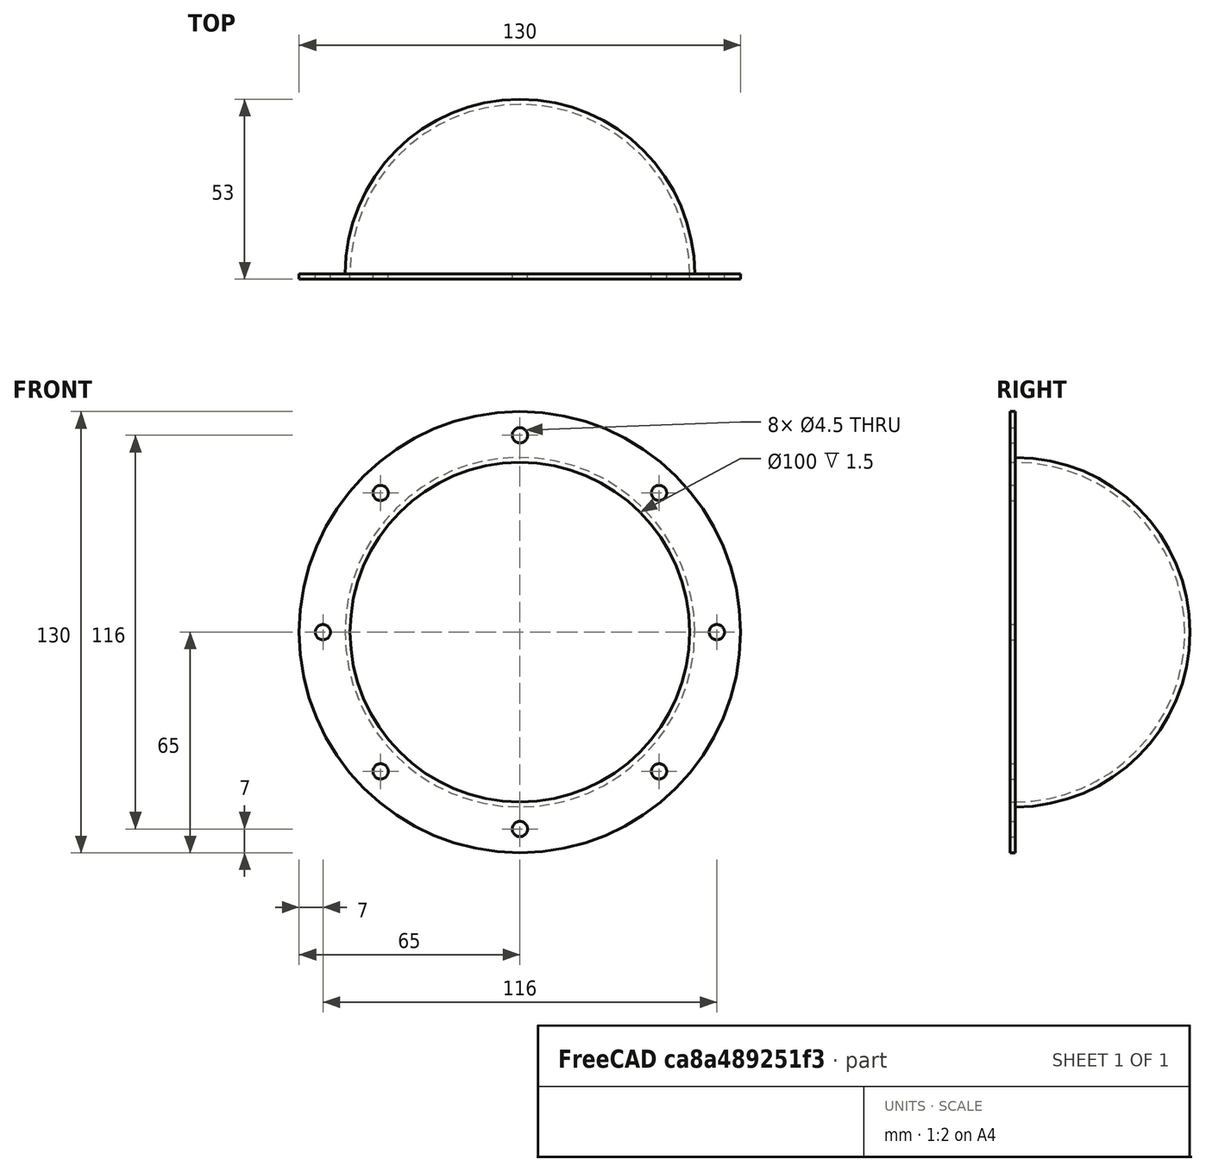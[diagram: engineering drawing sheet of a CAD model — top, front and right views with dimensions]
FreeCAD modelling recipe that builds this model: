
FCSTD DOCUMENT  (FreeCAD 0.18.4R)
Label: kuppel_LightDome
License: All rights reserved
LicenseURL: http://en.wikipedia.org/wiki/All_rights_reserved
objects: TechDraw::DrawViewDimension×4, TechDraw::DrawProjGroupItem×3, Sketcher::SketchObject×2, TechDraw::DrawSVGTemplate×2, TechDraw::DrawPage×2, Spreadsheet::Sheet×1, PartDesign::Revolution×1, TechDraw::DrawViewAnnotation×1, PartDesign::Hole×1, PartDesign::Body×1, TechDraw::DrawProjGroup×1, TechDraw::DrawViewPart×1, TechDraw::DrawGeomHatch×1
note: 7 computed .brp shape members not serialized (recipe doc carries the construction recipe); baked Part::Feature solids carry a one-line shape summary decoded from their .brp

FEATURE [Spreadsheet::Sheet] Spreadsheet  label="Parameterliste"
  cells = A1=Radius_Kuppel; B1=50; A2=Materialdicke; B2=1.5; A3=Radius_Boden_aussen; B3=65; A4=Radius_Boden_innen; B4=50; A5=Radius_Bohrkreis_aussen; B5=58; A6=Radius_Bohrloch_Schraube; B6=2; A7=Radius_Bohrloch_Dichtung; B7=1.5
FEATURE [Sketcher::SketchObject] Sketch
  MapMode = 5
  Support = -> [XY_Plane001]
  expr: Constraints[21] = Spreadsheet.B2
  expr: Constraints[19] = Spreadsheet.B1 + 2 * Spreadsheet.B2
  expr: Constraints[16] = Spreadsheet.B1
  expr: Constraints[1] = Spreadsheet.B2
  expr: Constraints[12] = Spreadsheet.B3
  expr: Constraints[2] = Spreadsheet.B1
  sketch-geometry (8):
    g0: LineSegment [constr] StartX=0 StartY=1.5 StartZ=0 EndX=50 EndY=1.50003 EndZ=0
    g1: LineSegment StartX=51.5 StartY=1.5 StartZ=0 EndX=65 EndY=1.5 EndZ=0
    g2: LineSegment StartX=65 StartY=1.5 StartZ=0 EndX=65 EndY=0 EndZ=0
    g3: LineSegment StartX=65 StartY=0 StartZ=0 EndX=50 EndY=0 EndZ=0
    g4: LineSegment StartX=50 StartY=0 StartZ=0 EndX=50 EndY=1.50003 EndZ=0
    g5: ArcOfCircle CenterX=0 CenterY=1.5 CenterZ=0 NormalX=0 NormalY=0 NormalZ=1 AngleXU=0 Radius=50 StartAngle=5.9196e-07 EndAngle=1.5708
    g6: ArcOfCircle CenterX=0 CenterY=1.5 CenterZ=0 NormalX=0 NormalY=0 NormalZ=1 AngleXU=0 Radius=51.5 StartAngle=1.09e-14 EndAngle=1.5708
    g7: LineSegment StartX=5.635e-13 StartY=53 StartZ=0 EndX=2.695e-13 EndY=51.5 EndZ=0
  constraints (24):
    c: PointOnObject(g0,g-2)
    c: DistanceY(g-1,g0) = 1.5
    c: DistanceX(g0,g0) = 50
    c: Coincident(g1,g2)
    c: Coincident(g2,g3)
    c: Coincident(g3,g4)
    c: Horizontal(g1)
    c: Horizontal(g3)
    c: Vertical(g2)
    c: Vertical(g4)
    c: Coincident(g4,g0)
    c: PointOnObject(g3,g-1)
    c: DistanceX(g-1,g2) = 65
    c: Coincident(g5,g0)
    c: PointOnObject(g5,g-2)
    c: Coincident(g5,g0)
    c: DistanceY(g0,g5) = 50
    c: Coincident(g6,g5)
    c: PointOnObject(g6,g-2)
    c: DistanceY(g-1,g6) = 53
    c: Coincident(g1,g6)
    c: DistanceY(g2) = 1.5
    c: Coincident(g7,g6)
    c: Coincident(g7,g5)
FEATURE [PartDesign::Revolution] Revolution
  Angle = 360
  Axis = (0,1,0)
  Base = (0,0,0)
  Profile = -> Sketch
  ReferenceAxis = -> Sketch [V_Axis]
  Reversed = true
FEATURE [TechDraw::DrawSVGTemplate] Template
  EditableTexts = AUTHOR_NAME=Norman Rembarz; DN=DN; DRAWING_TITLE=Kaufteil - Bearbeitungsplan; FC-DATE=28/10/2020; FC-REV=REV A; FC-SC=1:3; FC-SH=1/2; FC-SI=A4; FreeCAD_DRAWING=of light-dome module; PN=PN; SI-1=modification details; SI-3=REGREEN PROJECT of EU
  Height = 210
  Orientation = 1
  Width = 297
FEATURE [TechDraw::DrawViewAnnotation] Annotation
  Font = osifont
  LineSpace = 80
  LockPosition = false
  MaxWidth = -1
  Rotation = 0
  ScaleType = 0
  Text = Kaufteil Acrylkuppel | Kuppeldurchmesser ca. 100mm | Achtung! Bearbeitung der Löcher nur mit Fräser.
  TextSize = 5
  TextStyle = 0
  X = 214.835
  Y = 78.2158
FEATURE [Sketcher::SketchObject] Sketch001
  ExternalGeometry = -> [Revolution]
  MapMode = 5
  Placement = pos=(0,0,0) rot=(1,0,0;1.5708rad)
  Support = -> [Revolution]
  expr: Constraints[41] = Spreadsheet.B6
  expr: Constraints[38] = Spreadsheet.B6
  expr: Constraints[29] = Spreadsheet.B6
  expr: Constraints[26] = Spreadsheet.B6
  expr: Constraints[32] = Spreadsheet.B6
  expr: Constraints[4] = Spreadsheet.B6
  expr: Constraints[23] = Spreadsheet.B6
  expr: Constraints[11] = Spreadsheet.B3 * 2 + 20
  expr: Constraints.Bohrkreis_aussen = Spreadsheet.B5
  expr: Constraints[35] = Spreadsheet.B6
  expr: Constraints.Außenring = Spreadsheet.B3
  sketch-geometry (16):
    g0: Circle CenterX=0 CenterY=0 CenterZ=0 NormalX=0 NormalY=0 NormalZ=1 AngleXU=0 Radius=65
    g1: Circle [constr] CenterX=0 CenterY=0 CenterZ=0 NormalX=0 NormalY=0 NormalZ=1 AngleXU=0 Radius=58
    g2: Circle CenterX=0 CenterY=58 CenterZ=0 NormalX=0 NormalY=0 NormalZ=1 AngleXU=0 Radius=2
    g3: LineSegment [constr] StartX=75 StartY=75 StartZ=0 EndX=-75 EndY=75 EndZ=0
    g4: LineSegment [constr] StartX=-75 StartY=75 StartZ=0 EndX=-75 EndY=-75 EndZ=0
    g5: LineSegment [constr] StartX=-75 StartY=-75 StartZ=0 EndX=75 EndY=-75 EndZ=0
    g6: LineSegment [constr] StartX=75 StartY=-75 StartZ=0 EndX=75 EndY=75 EndZ=0
    g7: LineSegment [constr] StartX=75 StartY=75 StartZ=0 EndX=-75 EndY=-75 EndZ=0
    g8: LineSegment [constr] StartX=-80 StartY=80 StartZ=0 EndX=80 EndY=-80 EndZ=0
    g9: Circle CenterX=41.0122 CenterY=41.0122 CenterZ=0 NormalX=0 NormalY=0 NormalZ=1 AngleXU=0 Radius=2
    g10: Circle CenterX=58 CenterY=0 CenterZ=0 NormalX=0 NormalY=0 NormalZ=1 AngleXU=0 Radius=2
    g11: Circle CenterX=-41.0122 CenterY=41.0122 CenterZ=0 NormalX=0 NormalY=0 NormalZ=1 AngleXU=0 Radius=2
    g12: Circle CenterX=-58 CenterY=0 CenterZ=0 NormalX=0 NormalY=0 NormalZ=1 AngleXU=0 Radius=2
    g13: Circle CenterX=-41.0122 CenterY=-41.0122 CenterZ=0 NormalX=0 NormalY=0 NormalZ=1 AngleXU=0 Radius=2
    g14: Circle CenterX=0 CenterY=-58 CenterZ=0 NormalX=0 NormalY=0 NormalZ=1 AngleXU=0 Radius=2
    g15: Circle CenterX=41.0122 CenterY=-41.0122 CenterZ=0 NormalX=0 NormalY=0 NormalZ=1 AngleXU=0 Radius=2
  constraints (44):
    c: Radius(g0) = 65  'Außenring'
    c: Coincident(g0,g-1)
    c: Radius(g1) = 58  'Bohrkreis_aussen'
    c: Coincident(g1,g0)
    c: Radius(g2) = 2
    c: PointOnObject(g2,g1)
    c: PointOnObject(g2,g-2)
    c: Coincident(g3,g4)
    c: Coincident(g4,g5)
    c: Coincident(g5,g6)
    c: Coincident(g6,g3)
    c: DistanceY(g6,g6) = 150
    c: Equal(g3,g4)
    c: Equal(g4,g5)
    c: Equal(g5,g6)
    c: Symmetric(g5,g4,g-2)
    c: Symmetric(g3,g5,g-1)
    c: Coincident(g7,g4)
    c: Coincident(g7,g3)
    c: DistanceY(g-1,g8) = 80
    c: DistanceX(g8,g-1) = 80
    c: DistanceY(g8,g-1) = 80
    c: DistanceX(g-1,g8) = 80
    c: Radius(g9) = 2
    c: PointOnObject(g9,g7)
    c: PointOnObject(g9,g1)
    c: Radius(g10) = 2
    c: PointOnObject(g10,g-1)
    c: PointOnObject(g10,g1)
    c: Radius(g15) = 2
    c: PointOnObject(g15,g8)
    c: PointOnObject(g15,g1)
    c: Radius(g14) = 2
    c: PointOnObject(g14,g-2)
    c: PointOnObject(g14,g1)
    c: Radius(g13) = 2
    c: PointOnObject(g13,g7)
    c: PointOnObject(g13,g1)
    c: Radius(g12) = 2
    c: PointOnObject(g12,g-1)
    c: PointOnObject(g12,g1)
    c: Radius(g11) = 2
    c: PointOnObject(g11,g8)
    c: PointOnObject(g11,g1)
FEATURE [PartDesign::Hole] Hole
  BaseFeature = -> Revolution
  Depth = 25
  DepthType = 0
  Diameter = 4.5
  DrillPoint = 1
  DrillPointAngle = 118
  HoleCutCountersinkAngle = 90
  HoleCutDepth = 0
  HoleCutDiameter = 0
  HoleCutType = 0
  ModelActualThread = false
  Profile = -> Sketch001
  Tapered = false
  TaperedAngle = 90
  ThreadAngle = 0
  ThreadClass = 0
  ThreadCutOffInner = 0
  ThreadCutOffOuter = 0
  ThreadDirection = 0
  ThreadFit = 0
  ThreadPitch = 0
  ThreadSize = 0
  ThreadType = 0
  Threaded = false
  expr: Diameter = Spreadsheet.B6 * 2 + 0.5
FEATURE [PartDesign::Body] Body001  label="Kuppel_Acryl"
  Group = -> [Sketch,Revolution,Sketch001,Hole]
  Origin = -> Origin001
  Tip = -> Hole
FEATURE [TechDraw::DrawProjGroupItem] ProjItem  label="Seitenansicht"
  CoarseView = false
  Direction = (0,0,1)
  Focus = 100
  HardHidden = false
  IsoCount = 0
  IsoHidden = false
  IsoVisible = false
  LockPosition = true
  Perspective = false
  Rotation = 0
  RotationVector = (1,0,0)
  Scale = 2
  ScaleType = 2
  SeamHidden = false
  SeamVisible = false
  SmoothHidden = false
  SmoothVisible = false
  Source = -> [Body001]
  Type = 0
  X = 0
  Y = 0
FEATURE [TechDraw::DrawProjGroupItem] ProjItem001  label="Draufsicht"
  CoarseView = false
  Direction = (0,-1,0)
  Focus = 100
  HardHidden = false
  IsoCount = 0
  IsoHidden = false
  IsoVisible = false
  LockPosition = false
  Perspective = false
  Rotation = 0
  RotationVector = (1,0,0)
  Scale = 0.35
  ScaleType = 2
  SeamHidden = false
  SeamVisible = false
  SmoothHidden = false
  SmoothVisible = false
  Source = -> [Body001]
  Type = 5
  X = 0
  Y = 80
FEATURE [TechDraw::DrawProjGroupItem] ProjItem002  label="Iso-Ansicht"
  CoarseView = false
  Direction = (-1,-1,1)
  Focus = 100
  HardHidden = false
  IsoCount = 0
  IsoHidden = false
  IsoVisible = false
  LockPosition = false
  Perspective = false
  Rotation = 0
  RotationVector = (1,0,1)
  Scale = 0.5
  ScaleType = 2
  SeamHidden = false
  SeamVisible = false
  SmoothHidden = false
  SmoothVisible = false
  Source = -> [Body001]
  Type = 8
  X = 80
  Y = 80
FEATURE [TechDraw::DrawProjGroup] ProjGroup
  Anchor = -> ProjItem
  AutoDistribute = true
  LockPosition = false
  ProjectionType = 0
  Rotation = 0
  Scale = 0.5
  ScaleType = 1
  Source = -> [Body001]
  Views = -> [ProjItem,ProjItem001,ProjItem002]
  X = 66.0524
  Y = 72.7791
  spacingX = 15
  spacingY = 15
FEATURE [TechDraw::DrawViewDimension] Dimension
  Arbitrary = false
  FormatSpec = ⌀%.2f
  LockPosition = false
  MeasureType = 1
  OverTolerance = 0
  References2D = -> [ProjItem001]
  Rotation = 0
  ScaleType = 0
  Type = 5
  UnderTolerance = 0
  X = 58.7269
  Y = -41.1317
FEATURE [TechDraw::DrawViewDimension] Dimension001
  Arbitrary = false
  FormatSpec = ⌀%.2f
  LockPosition = false
  MeasureType = 1
  OverTolerance = 0
  References2D = -> [ProjItem001]
  Rotation = 0
  ScaleType = 0
  Type = 5
  UnderTolerance = 0
  X = -1.59818
  Y = -12.0056
FEATURE [TechDraw::DrawViewDimension] Dimension002
  Arbitrary = false
  FormatSpec = ⌀%.2f
  LockPosition = false
  MeasureType = 1
  OverTolerance = 0
  References2D = -> [ProjItem]
  Rotation = 0
  ScaleType = 0
  Type = 5
  UnderTolerance = 0
  X = 60.3645
  Y = 7.42655
FEATURE [TechDraw::DrawViewDimension] Dimension003
  Arbitrary = false
  FormatSpec = %.2f
  LockPosition = false
  MeasureType = 1
  OverTolerance = 0
  References2D = -> [ProjItem]
  Rotation = 0
  ScaleType = 0
  Type = 2
  UnderTolerance = 0
  X = 72.6003
  Y = -3.91178
FEATURE [TechDraw::DrawPage] Page  label="Zeichnung_Kuppel_m_Löchern"
  KeepUpdated = true
  ProjectionType = 0
  Template = -> Template
  Views = -> [ProjGroup,Dimension,Dimension001,Dimension002,Dimension003,Annotation]
FEATURE [TechDraw::DrawSVGTemplate] Template001
  EditableTexts = AUTHOR_NAME=Norman Rembarz; DN=DN; DRAWING_TITLE=Kaufteil - Bearbeitung; FC-DATE=28/10/2020; FC-REV=REV A; FC-SC=1:1; FC-SH=2/2; FC-SI=A4; FreeCAD_DRAWING=Bohrschablone; PN=PN; SI-3=REGREEN PROJECT of EU
  Height = 210
  Orientation = 1
  Width = 297
FEATURE [TechDraw::DrawViewPart] View  label="Draufsicht001"
  CoarseView = false
  Direction = (-0.031,0.999,0.034)
  Focus = 100
  HardHidden = false
  IsoCount = 0
  IsoHidden = false
  IsoVisible = false
  LockPosition = false
  Perspective = false
  Rotation = 0
  ScaleType = 0
  SeamHidden = false
  SeamVisible = false
  SmoothHidden = false
  SmoothVisible = false
  Source = -> [Body001]
  X = 148.5
  Y = 118.822
FEATURE [TechDraw::DrawPage] Page001  label="Schablone"
  KeepUpdated = true
  ProjectionType = 0
  Template = -> Template001
  Views = -> [View]
FEATURE [TechDraw::DrawGeomHatch] GeomHatch  label="GeomHatchFX1"
  FilePattern = /Applications/FreeCAD.app/Contents/Resources/data/Mod/TechDraw/PAT/FCPAT.pat
  NamePattern = Diamond
  ScalePattern = 1
  Source = -> View [Face1]
